# Revit family: Metal_Lockers-Salsbury_Industries-S_61000_Series-1_Wide_Units
name_source: partatom
category: Specialty Equipment
revit_build: Autodesk Revit 2016 (Build: 20150714_1515(x64)
units: mm (PartAtom-declared; Revit-internal decimal feet)

## family parameters
Always vertical = Yes
Cut with Voids When Loaded = No
OmniClass Number = 23.40.00.00
OmniClass Title = Equipment and Furnishings
Part Type = Normal
Room Calculation Point = No
Round Connector Dimension = Use Diameter
Shared = No
Work Plane-Based = No

## types (18) — shared parameters
Assembly Code = C1030310
Hasp Handle Material = Plastic - Salsbury Finish - Black
Hasp Plate Rivet Material = Steel -Salsbury Finish - Polished Steel
Manufacturer = Salsbury Industries
MasterFormat Number = 10 51 13
MasterFormat Title = Lockers
OmniClass 23 Number = 23.40.00.00
OmniClass 23 Title = Equipment and Furnishings
Type Comments = See-Through Metal Locker - Single Tier
URL = www.lockers.com
Version = 3.0 (03/30/18)
Width = 12.04 "
Window Panel Material = Polycarbonate - Salsbury Finish - Clear

## per-type parameters (varying)
| type | Base Height | Depth | Description | Door Location D1 | Door Window Height | Door Window Offset | Model | Sloping Hood Height | Standard Leg Base | Unit Height | Zee Base |
| S-61162 - with Standard 6" High Legs | 6 " | 12.01 " | 1 Wide - 6 Feet High - 12 Inches Deep | See-Through Metal Locker Doors-12 inch with Hasps : Single Tier Door - 6 foot | 26.25 " | 3.84 " | S-61162 | 6.625 " | Metal Locker Legs : 6" High - 12" W x 12" D | 72 " | Metal Locker Zee Base : None |
| S-61165 - with Standard 6" High Legs | 6 " | 15.01 " | 1 Wide - 6 Feet High - 15 Inches Deep | See-Through Metal Locker Doors-12 inch with Hasps : Single Tier Door - 6 foot | 26.25 " | 3.84 " | S-61165 | 8.682 " | Metal Locker Legs : 6" High - 12" W x 15" D | 72 " | Metal Locker Zee Base : None |
| S-61168 - with Standard 6" High Legs | 6 " | 18.01 " | 1 Wide - 6 Feet High - 18 Inches Deep | See-Through Metal Locker Doors-12 inch with Hasps : Single Tier Door - 6 foot | 26.25 " | 3.84 " | S-61168 | 10.739 " | Metal Locker Legs : 6" High - 12"W x 18"D | 72 " | Metal Locker Zee Base : None |
| S-61162 - with 77572 Zee Base and 77550 Lockers without Legs | 4 " | 12.01 " | 1 Wide - 6 Feet High - 12 Inches Deep with Zee Base and Lockers without Legs | See-Through Metal Locker Doors-12 inch with Hasps : Single Tier Door - 6 foot | 26.25 " | 3.84 " | S-61162 with 77572 and 77550 | 6.625 " | Metal Locker Legs : No Legs | 72 " | Metal Locker Zee Base : 77572- 12" W x 12" D |
| S-61165 - with 77575 Zee Base and 77550 Lockers without Legs | 4 " | 15.01 " | 1 Wide - 6 Feet High - 15 Inches Deep with Zee Base and Lockers without Legs | See-Through Metal Locker Doors-12 inch with Hasps : Single Tier Door - 6 foot | 26.25 " | 3.84 " | S-61165 with 77575 and 77550 | 8.682 " | Metal Locker Legs : No Legs | 72 " | Metal Locker Zee Base : 77575 - 12" W x 15" D |
| S-61168 - with 77578 Zee Base and 77550 Lockers without Legs | 4 " | 18.01 " | 1 Wide - 6 Feet High - 18 Inches Deep with Zee Base and Lockers without Legs | See-Through Metal Locker Doors-12 inch with Hasps : Single Tier Door - 6 foot | 26.25 " | 3.84 " | S-61168 with 77578 and 77550 | 10.739 " | Metal Locker Legs : No Legs | 72 " | Metal Locker Zee Base : 77578 - 12"W x 18"D |
| S-61162 - with 77550 Lockers without Legs | 0 " | 12.01 " | 1 Wide - 6 Feet High - 12 Inches Deep with Lockers without Legs | See-Through Metal Locker Doors-12 inch with Hasps : Single Tier Door - 6 foot | 26.25 " | 3.84 " | S-61162 with 77550 | 6.625 " | Metal Locker Legs : No Legs | 72 " | Metal Locker Zee Base : None |
| S-61165 - with 77550 Lockers without Legs | 0 " | 15.01 " | 1 Wide - 6 Feet High - 15 Inches Deep with Lockers without Legs | See-Through Metal Locker Doors-12 inch with Hasps : Single Tier Door - 6 foot | 26.25 " | 3.84 " | S-61165 with 77550 | 8.682 " | Metal Locker Legs : No Legs | 72 " | Metal Locker Zee Base : None |
| S-61168 - with 77550 Lockers without Legs | 0 " | 18.01 " | 1 Wide - 6 Feet High - 18 Inches Deep with Lockers without Legs | See-Through Metal Locker Doors-12 inch with Hasps : Single Tier Door - 6 foot | 26.25 " | 3.84 " | S-61168 with 77550 | 10.739 " | Metal Locker Legs : No Legs | 72 " | Metal Locker Zee Base : None |
| S-61152 - with Standard 6" High Legs | 6 " | 12.01 " | 1 Wide - 5 Feet High - 12 Inches Deep | See-Through Metal Locker Doors-12 inch with Hasps : Single Tier Door - 5 foot | 20.25 " | 4.153 " | S-61152 | 6.625 " | Metal Locker Legs : 6" High - 12" W x 12" D | 60 " | Metal Locker Zee Base : None |
| S-61152 - with 77572 Zee Base and 77550 Lockers without Legs | 4 " | 12.01 " | 1 Wide - 5 Feet High - 12 Inches Deep with Zee Base and Lockers without Legs | See-Through Metal Locker Doors-12 inch with Hasps : Single Tier Door - 5 foot | 20.25 " | 4.153 " | S-61152 with 77572 and 77550 | 6.625 " | Metal Locker Legs : No Legs | 60 " | Metal Locker Zee Base : 77572- 12" W x 12" D |
| S-61152 - with 77550 Lockers without Legs | 0 " | 12.01 " | 1 Wide - 5 Feet High - 12 Inches Deep with Lockers without Legs | See-Through Metal Locker Doors-12 inch with Hasps : Single Tier Door - 5 foot | 20.25 " | 4.153 " | S-61152 with 77550 | 6.625 " | Metal Locker Legs : No Legs | 60 " | Metal Locker Zee Base : None |
| S-61155 - with Standard 6" High Legs | 6 " | 15.01 " | 1 Wide - 5 Feet High - 15 Inches Deep | See-Through Metal Locker Doors-12 inch with Hasps : Single Tier Door - 5 foot | 20.25 " | 4.153 " | S-61155 | 8.682 " | Metal Locker Legs : 6" High - 12" W x 15" D | 60 " | Metal Locker Zee Base : None |
| S-61155 - with 77575 Zee Base and 77550 Lockers without Legs | 4 " | 15.01 " | 1 Wide - 5 Feet High - 15 Inches Deep with Zee Base and Lockers without Legs | See-Through Metal Locker Doors-12 inch with Hasps : Single Tier Door - 5 foot | 20.25 " | 4.153 " | S-61155 with 77575 and 77550 | 8.682 " | Metal Locker Legs : No Legs | 60 " | Metal Locker Zee Base : 77575 - 12" W x 15" D |
| S-61155 - with 77550 Lockers without Legs | 0 " | 15.01 " | 1 Wide - 5 Feet High - 15 Inches Deep with Lockers without Legs | See-Through Metal Locker Doors-12 inch with Hasps : Single Tier Door - 5 foot | 20.25 " | 4.153 " | S-61155 with 77550 | 8.682 " | Metal Locker Legs : No Legs | 60 " | Metal Locker Zee Base : None |
| S-61158 - with Standard 6" High Legs | 6 " | 18.01 " | 1 Wide - 5 Feet High - 18 Inches Deep | See-Through Metal Locker Doors-12 inch with Hasps : Single Tier Door - 5 foot | 20.25 " | 4.153 " | S-61158 | 10.739 " | Metal Locker Legs : 6" High - 12"W x 18"D | 60 " | Metal Locker Zee Base : None |
| S-61158 - with 77578 Zee Base and 77550 Lockers without Legs | 4 " | 18.01 " | 1 Wide - 5 Feet High - 18 Inches Deep with Zee Base and Lockers without Legs | See-Through Metal Locker Doors-12 inch with Hasps : Single Tier Door - 5 foot | 20.25 " | 4.153 " | S-61158 with 77578 and 77550 | 10.739 " | Metal Locker Legs : No Legs | 60 " | Metal Locker Zee Base : 77578 - 12"W x 18"D |
| S-61158 - with 77550 Lockers without Legs | 0 " | 18.01 " | 1 Wide - 5 Feet High - 18 Inches Deep with Lockers without Legs | See-Through Metal Locker Doors-12 inch with Hasps : Single Tier Door - 5 foot | 20.25 " | 4.153 " | S-61158 with 77550 | 10.739 " | Metal Locker Legs : No Legs | 60 " | Metal Locker Zee Base : None |

## geometry (parser evidence)
native form markers: Sweep x36
no freeform markers — native parametric forms only
